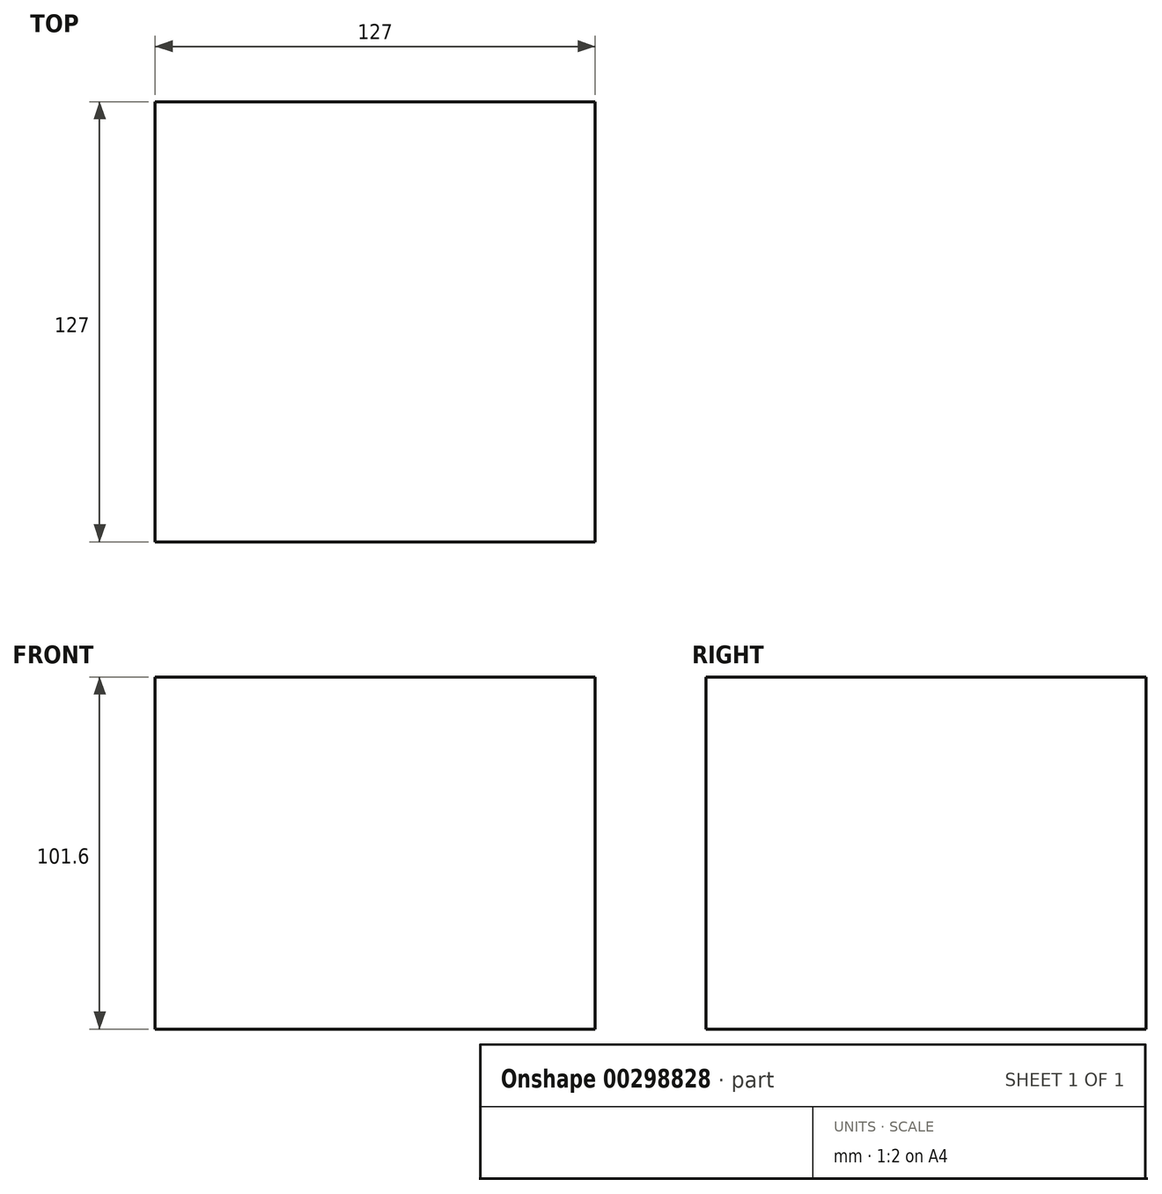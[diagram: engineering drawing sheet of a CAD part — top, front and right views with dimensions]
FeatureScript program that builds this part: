
annotation { "Feature Type Name" : "Feature", "Feature Type Description" : "" }
export const myFeature = defineFeature(function(context is Context, id is Id, definition is map)
    precondition{}
    {
        {
            var Q0;
            Q0=qCreatedBy(makeId("Top.planeOp"),FACE);
            var sketch = newSketch(context, id + "F0", { "sketchPlane" : qUnion([Q0])});
            skLineSegment(sketch, "E0.bottom", {"start": v(-75.84, 76.12) * mm, "end": v(51.16, 76.12) * mm});
            skLineSegment(sketch, "E0.top", {"start": v(-75.84, -50.88) * mm, "end": v(51.16, -50.88) * mm});
            skLineSegment(sketch, "E0.left", {"start": v(-75.84, 76.12) * mm, "end": v(-75.84, -50.88) * mm});
            skLineSegment(sketch, "E0.right", {"start": v(51.16, 76.12) * mm, "end": v(51.16, -50.88) * mm});
            skSolve(sketch);
        }
        {
            var Q0;
            Q0=makeQuery(id+"F0.imprint","IMPRINT",FACE,{"disambiguationData":[TD([[makeQuery(id+"F0.imprint","IMPRINT",EDGE,{"derivedFrom":sQuery(id+"F0.wireOp",EDGE,"E0.bottom")}),-1.0]])]});
            var sketch = newSketch(context, id + "F1", { "sketchPlane" : qUnion([Q0])});
            skLineSegment(sketch, "E1", {"start": v(-25.02, 75.94) * mm, "end": v(-75.82, 25.14) * mm});
            skLineSegment(sketch, "E2", {"start": v(-75.82, 25.14) * mm, "end": v(-75.82, 75.94) * mm});
            skLineSegment(sketch, "E3", {"start": v(-75.82, 75.94) * mm, "end": v(-25.02, 75.94) * mm});
            skLineSegment(sketch, "E4", {"start": v(0.1, -50.68) * mm, "end": v(50.9, -0.13) * mm});
            skLineSegment(sketch, "E5", {"start": v(50.9, -0.13) * mm, "end": v(50.9, -50.93) * mm});
            skLineSegment(sketch, "E6", {"start": v(50.9, -50.93) * mm, "end": v(0.1, -50.68) * mm});
            skSolve(sketch);
        }
        {
            var Q0;
            Q0=makeQuery(id+"F0.imprint","IMPRINT",FACE,{"disambiguationData":[TD([[makeQuery(id+"F0.imprint","IMPRINT",EDGE,{"derivedFrom":sQuery(id+"F0.wireOp",EDGE,"E0.bottom")}),-1.0]])]});
            extrude(context, id + "F2", {"entities" : qUnion([Q0]), "depth" : 101.6 * mm});
        }
        {
            var Q0;
            {var subQ0=sQuery(id+"F1.wireOp",EDGE,"E6");var subQ1=sQuery(id+"F1.wireOp",EDGE,"E5");var subQ2=makeQuery(id+"F1.imprint","INTERSECT",VERTEX,{"derivedFrom":[subQ1,subQ0]});Q0=makeQuery(id+"F1.imprint","IMPRINT",FACE,{"disambiguationData":[TD([[makeQuery(id+"F1.imprint","IMPRINT",EDGE,{"disambiguationData":[TD([[subQ2,1.0]])],"derivedFrom":subQ1}),-1.0]])]});}
            extrude(context, id + "F3", {"entities" : qUnion([Q0]), "operationType" : NewBodyOperationType.REMOVE, "oppositeDirection" : true, "depth" : 25.4 * mm});
        }
    });
